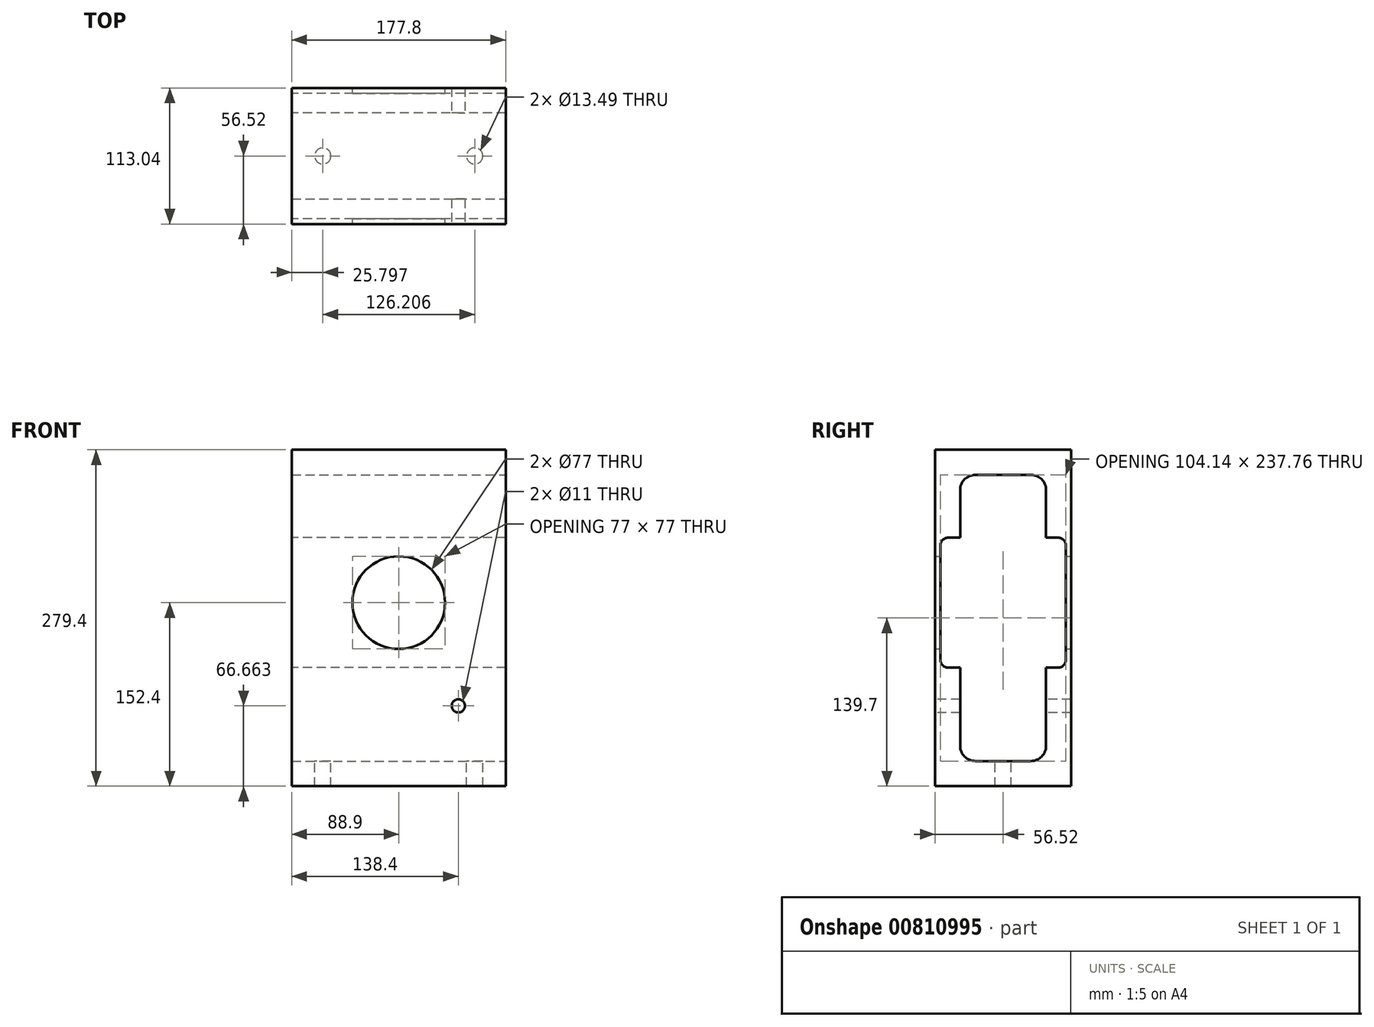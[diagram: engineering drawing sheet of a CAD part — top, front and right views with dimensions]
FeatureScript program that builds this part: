
annotation { "Feature Type Name" : "Feature", "Feature Type Description" : "" }
export const myFeature = defineFeature(function(context is Context, id is Id, definition is map)
    precondition{}
    {
        {
            var Q0;
            Q0=qCreatedBy(makeId("Front.planeOp"),FACE);
            var sketch = newSketch(context, id + "F0", { "sketchPlane" : qUnion([Q0])});
            skCircle(sketch, "E0", {"center": v(0, 0) * mm, "radius": 38.5 * mm});
            skLineSegment(sketch, "E1.bottom", {"start": v(-88.9, 127) * mm, "end": v(88.9, 127) * mm});
            skLineSegment(sketch, "E1.top", {"start": v(-88.9, -152.4) * mm, "end": v(88.9, -152.4) * mm});
            skLineSegment(sketch, "E1.left", {"start": v(-88.9, 127) * mm, "end": v(-88.9, -152.4) * mm});
            skLineSegment(sketch, "E1.right", {"start": v(88.9, 127) * mm, "end": v(88.9, -152.4) * mm});
            skLineSegment(sketch, "E2", {"start": v(0, 0) * mm, "end": v(0, 127) * mm, "construction": true});
            skSolve(sketch);
        }
        {
            var Q0;
            Q0 = qSketchRegion(id + "F0", true);
            extrude(context, id + "F1", {"entities" : qUnion([Q0]), "depth" : 113.03 * mm, "offsetDistance" : 25.4 * mm, "symmetric" : true});
        }
        {
            var Q0;
            Q0=makeQuery(id+"F1.opExtrude","SWEPT_FACE",FACE,{"disambiguationData":[OSD([sQuery(id+"F0.wireOp",EDGE,"E1.right")])]});
            var sketch = newSketch(context, id + "F2", { "sketchPlane" : qUnion([Q0])});
            skLineSegment(sketch, "E3.0", {"start": v(35.7, -118.88) * mm, "end": v(35.7, 93.48) * mm});
            skLineSegment(sketch, "E3.1", {"start": v(-23, -131.58) * mm, "end": v(23, -131.58) * mm});
            skLineSegment(sketch, "E3.2", {"start": v(-35.7, 93.48) * mm, "end": v(-35.7, -118.88) * mm});
            skLineSegment(sketch, "E3.3", {"start": v(23, 106.18) * mm, "end": v(-23, 106.18) * mm});
            skPoint(sketch, "E4.visualSharp", {"position": v(-35.7, 106.18) * mm});
            skArc(sketch, "E4.filletArc", {"start": v(-23, 106.18) * mm, "mid": v(-31.97, 102.46) * mm, "end": v(-35.7, 93.48) * mm});
            skPoint(sketch, "E5.visualSharp", {"position": v(35.7, 106.18) * mm});
            skArc(sketch, "E5.filletArc", {"start": v(35.7, 93.48) * mm, "mid": v(31.97, 102.46) * mm, "end": v(23, 106.18) * mm});
            skPoint(sketch, "E6.visualSharp", {"position": v(35.7, -131.58) * mm});
            skArc(sketch, "E6.filletArc", {"start": v(23, -131.58) * mm, "mid": v(31.97, -127.86) * mm, "end": v(35.7, -118.88) * mm});
            skPoint(sketch, "E7.visualSharp", {"position": v(-35.7, -131.58) * mm});
            skArc(sketch, "E7.filletArc", {"start": v(-35.7, -118.88) * mm, "mid": v(-31.97, -127.86) * mm, "end": v(-23, -131.58) * mm});
            skSolve(sketch);
        }
        {
            var Q0;
            Q0=makeQuery(id+"F2.imprint","IMPRINT",FACE,{"disambiguationData":[TD([[makeQuery(id+"F2.imprint","IMPRINT",EDGE,{"derivedFrom":sQuery(id+"F2.wireOp",EDGE,"E3.0")}),1.0]])]});
            extrude(context, id + "F3", {"entities" : qUnion([Q0]), "operationType" : NewBodyOperationType.REMOVE, "endBound" : BoundingType.THROUGH_ALL, "oppositeDirection" : true, "depth" : 25.4 * mm, "offsetDistance" : 25.4 * mm});
        }
        {
            var Q0;
            Q0=makeQuery(id+"F1.opExtrude","SWEPT_FACE",FACE,{"disambiguationData":[OSD([sQuery(id+"F0.wireOp",EDGE,"E1.left")])]});
            var sketch = newSketch(context, id + "F4", { "sketchPlane" : qUnion([Q0])});
            skLineSegment(sketch, "E8.bottom", {"start": v(-45.72, 53.97) * mm, "end": v(45.72, 53.97) * mm});
            skLineSegment(sketch, "E8.top", {"start": v(-45.72, -53.98) * mm, "end": v(45.72, -53.98) * mm});
            skLineSegment(sketch, "E8.left", {"start": v(-52.07, 47.62) * mm, "end": v(-52.07, -47.63) * mm});
            skLineSegment(sketch, "E8.right", {"start": v(52.07, 47.62) * mm, "end": v(52.07, -47.62) * mm});
            skLineSegment(sketch, "E9", {"start": v(-52.07, 53.98) * mm, "end": v(52.07, -53.98) * mm, "construction": true});
            skPoint(sketch, "E10.visualSharp", {"position": v(-52.07, 53.97) * mm});
            skArc(sketch, "E10.filletArc", {"start": v(-45.72, 53.97) * mm, "mid": v(-50.21, 52.12) * mm, "end": v(-52.07, 47.62) * mm});
            skPoint(sketch, "E11.visualSharp", {"position": v(52.07, 53.97) * mm});
            skArc(sketch, "E11.filletArc", {"start": v(52.07, 47.62) * mm, "mid": v(50.21, 52.12) * mm, "end": v(45.72, 53.97) * mm});
            skPoint(sketch, "E12.visualSharp", {"position": v(52.07, -53.98) * mm});
            skArc(sketch, "E12.filletArc", {"start": v(45.72, -53.98) * mm, "mid": v(50.21, -52.12) * mm, "end": v(52.07, -47.62) * mm});
            skPoint(sketch, "E13.visualSharp", {"position": v(-52.07, -53.98) * mm});
            skArc(sketch, "E13.filletArc", {"start": v(-52.07, -47.63) * mm, "mid": v(-50.21, -52.12) * mm, "end": v(-45.72, -53.98) * mm});
            skSolve(sketch);
        }
        {
            var Q0;
            Q0 = qSketchRegion(id + "F4", true);
            extrude(context, id + "F5", {"entities" : qUnion([Q0]), "operationType" : NewBodyOperationType.REMOVE, "endBound" : BoundingType.THROUGH_ALL, "oppositeDirection" : true, "depth" : 25.4 * mm, "offsetDistance" : 25.4 * mm});
        }
        {
            var Q0;
            Q0=makeQuery(id+"F3.boolean.opBoolean","COPY",FACE,{"derivedFrom":makeQuery(id+"F3.opExtrude","SWEPT_FACE",FACE,{"disambiguationData":[OSD([sQuery(id+"F2.wireOp",EDGE,"E3.1")])]})});
            var sketch = newSketch(context, id + "F6", { "sketchPlane" : qUnion([Q0])});
            skLineSegment(sketch, "E14", {"start": v(88.9, 0) * mm, "end": v(-88.9, 0) * mm, "construction": true});
            skCircle(sketch, "E15", {"center": v(63.1, 0) * mm, "radius": 6.75 * mm});
            skCircle(sketch, "E16", {"center": v(-63.1, 0) * mm, "radius": 6.75 * mm});
            skCircle(sketch, "E17", {"center": v(0, 0) * mm, "radius": 63.1 * mm, "construction": true});
            skSolve(sketch);
        }
        {
            var Q0;
            Q0 = qSketchRegion(id + "F6", true);
            extrude(context, id + "F7", {"entities" : qUnion([Q0]), "operationType" : NewBodyOperationType.REMOVE, "endBound" : BoundingType.THROUGH_ALL, "oppositeDirection" : true, "depth" : 25.4 * mm, "offsetDistance" : 25.4 * mm});
        }
        {
            var Q0;
            Q0=makeQuery(id+"F1.opExtrude","CAP_FACE",FACE,{"disambiguationData":[OSD([sQuery(id+"F0.wireOp",EDGE,"E0"),sQuery(id+"F0.wireOp",EDGE,"E1.bottom"),sQuery(id+"F0.wireOp",EDGE,"E1.top"),sQuery(id+"F0.wireOp",EDGE,"E1.left"),sQuery(id+"F0.wireOp",EDGE,"E1.right")])],"isStart":false});
            var sketch = newSketch(context, id + "F8", { "sketchPlane" : qUnion([Q0])});
            skCircle(sketch, "E18", {"center": v(0, 0) * mm, "radius": 99 * mm, "construction": true});
            skCircle(sketch, "E19", {"center": v(49.5, -85.74) * mm, "radius": 5.5 * mm});
            skLineSegment(sketch, "E20", {"start": v(0, 0) * mm, "end": v(49.5, -85.74) * mm, "construction": true});
            skLineSegment(sketch, "E21", {"start": v(0, 0) * mm, "end": v(0, -99) * mm});
            skSolve(sketch);
        }
        {
            var Q0;
            Q0 = qSketchRegion(id + "F8", true);
            extrude(context, id + "F9", {"entities" : qUnion([Q0]), "operationType" : NewBodyOperationType.REMOVE, "endBound" : BoundingType.THROUGH_ALL, "oppositeDirection" : true, "depth" : 25.4 * mm, "offsetDistance" : 25.4 * mm});
        }
    });
